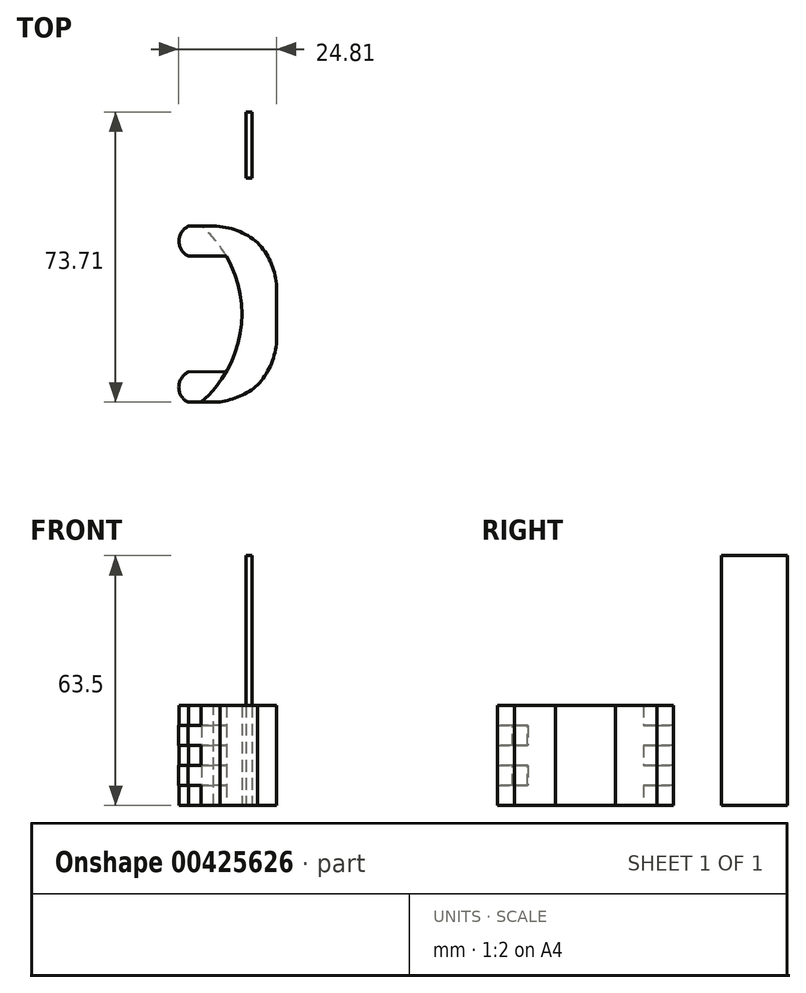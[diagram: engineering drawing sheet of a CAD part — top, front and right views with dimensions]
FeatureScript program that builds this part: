
annotation { "Feature Type Name" : "Feature", "Feature Type Description" : "" }
export const myFeature = defineFeature(function(context is Context, id is Id, definition is map)
    precondition{}
    {
        {
            var Q0;
            Q0=qCreatedBy(makeId("Top.planeOp"),FACE);
            var sketch = newSketch(context, id + "F0", { "sketchPlane" : qUnion([Q0])});
            skLineSegment(sketch, "E0.bottom", {"start": v(-27.3, 5.1) * mm, "end": v(-25.7, 5.1) * mm});
            skLineSegment(sketch, "E0.top", {"start": v(-27.3, -11.7) * mm, "end": v(-25.7, -11.7) * mm});
            skLineSegment(sketch, "E0.left", {"start": v(-27.3, 5.1) * mm, "end": v(-27.3, -11.7) * mm});
            skLineSegment(sketch, "E0.right", {"start": v(-25.7, 5.1) * mm, "end": v(-25.7, -11.7) * mm});
            skSolve(sketch);
        }
        {
            var Q0;
            Q0=makeQuery(id+"F0.imprint","IMPRINT",FACE,{"disambiguationData":[TD([[makeQuery(id+"F0.imprint","IMPRINT",EDGE,{"derivedFrom":sQuery(id+"F0.wireOp",EDGE,"E0.bottom")}),-1.0]])]});
            extrude(context, id + "F1", {"entities" : qUnion([Q0]), "depth" : 63.5 * mm});
        }
        {
            var Q0;
            Q0=qCreatedBy(makeId("Top.planeOp"),FACE);
            var sketch = newSketch(context, id + "F2", { "sketchPlane" : qUnion([Q0])});
            skArc(sketch, "E1", {"start": v(-38.65, -68.58) * mm, "mid": v(-28.33, -46.25) * mm, "end": v(-38.59, -23.9) * mm});
            skLineSegment(sketch, "E2", {"start": v(-28.33, -46.53) * mm, "end": v(-37.98, -46.37) * mm});
            skPoint(sketch, "E2.startSnap0", {"position": v(-38.5, -46.53) * mm});
            skPoint(sketch, "E2.endSnap0", {"position": v(-37.98, -46.54) * mm});
            skLineSegment(sketch, "E3", {"start": v(-29.06, -23.9) * mm, "end": v(-19.55, -32.32) * mm});
            skLineSegment(sketch, "E4", {"start": v(-29.13, -68.46) * mm, "end": v(-19.6, -60.08) * mm});
            skLineSegment(sketch, "E5", {"start": v(-38.59, -23.9) * mm, "end": v(-29.06, -23.9) * mm});
            skArc(sketch, "E6", {"start": v(-160.47, -81.65) * mm, "mid": v(-150.15, -59.32) * mm, "end": v(-160.4, -36.97) * mm});
            skLineSegment(sketch, "E7", {"start": v(-150.15, -59.6) * mm, "end": v(-159.8, -59.44) * mm});
            skPoint(sketch, "E7.startSnap0", {"position": v(-160.31, -59.6) * mm});
            skPoint(sketch, "E7.endSnap0", {"position": v(-159.8, -59.6) * mm});
            skLineSegment(sketch, "E8", {"start": v(-141.36, -36.97) * mm, "end": v(-141.42, -81.42) * mm});
            skLineSegment(sketch, "E9", {"start": v(-160.47, -81.65) * mm, "end": v(-141.42, -81.42) * mm});
            skLineSegment(sketch, "E10", {"start": v(-150.88, -36.97) * mm, "end": v(-141.37, -45.39) * mm});
            skLineSegment(sketch, "E11", {"start": v(-150.95, -81.53) * mm, "end": v(-141.4, -73.15) * mm});
            skLineSegment(sketch, "E12", {"start": v(-160.4, -36.97) * mm, "end": v(-150.88, -36.97) * mm});
            skLineSegment(sketch, "E13", {"start": v(-38.65, -68.58) * mm, "end": v(-29.13, -68.46) * mm});
            skLineSegment(sketch, "E14", {"start": v(-19.6, -60.08) * mm, "end": v(-19.55, -32.32) * mm});
            skSolve(sketch);
        }
        {
            var Q0;
            Q0=makeQuery(id+"F2.imprint","IMPRINT",FACE,{"disambiguationData":[TD([[makeQuery(id+"F2.imprint","IMPRINT",EDGE,{"derivedFrom":sQuery(id+"F2.wireOp",EDGE,"E3")}),-1.0]])]});
            extrude(context, id + "F3", {"entities" : qUnion([Q0]), "depth" : 25.4 * mm});
        }
        {
            var Q0;
            Q0=makeQuery(id+"F3.opExtrude","SWEPT_FACE",FACE,{"disambiguationData":[OSD([sQuery(id+"F2.wireOp",EDGE,"E13")])]});
            var sketch = newSketch(context, id + "F4", { "sketchPlane" : qUnion([Q0])});
            skLineSegment(sketch, "E15.bottom", {"start": v(-29.92, 25.4) * mm, "end": v(-45.16, 25.4) * mm});
            skLineSegment(sketch, "E15.top", {"start": v(-29.92, 20.32) * mm, "end": v(-45.16, 20.32) * mm});
            skLineSegment(sketch, "E15.left", {"start": v(-29.92, 25.4) * mm, "end": v(-29.92, 20.32) * mm});
            skLineSegment(sketch, "E15.right", {"start": v(-45.16, 25.4) * mm, "end": v(-45.16, 20.32) * mm});
            skLineSegment(sketch, "E16.top", {"start": v(-29.92, 15.24) * mm, "end": v(-45.16, 15.24) * mm});
            skLineSegment(sketch, "E16.left", {"start": v(-29.92, 20.32) * mm, "end": v(-29.92, 15.24) * mm});
            skLineSegment(sketch, "E16.right", {"start": v(-45.16, 20.32) * mm, "end": v(-45.16, 15.24) * mm});
            skLineSegment(sketch, "E17.top", {"start": v(-29.92, 10.16) * mm, "end": v(-45.16, 10.16) * mm});
            skLineSegment(sketch, "E17.left", {"start": v(-29.92, 15.24) * mm, "end": v(-29.92, 10.16) * mm});
            skLineSegment(sketch, "E17.right", {"start": v(-45.16, 15.24) * mm, "end": v(-45.16, 10.16) * mm});
            skLineSegment(sketch, "E18.top", {"start": v(-29.92, 5.08) * mm, "end": v(-45.16, 5.08) * mm});
            skLineSegment(sketch, "E18.left", {"start": v(-29.92, 10.16) * mm, "end": v(-29.92, 5.08) * mm});
            skLineSegment(sketch, "E18.right", {"start": v(-45.16, 10.16) * mm, "end": v(-45.16, 5.08) * mm});
            skLineSegment(sketch, "E19.top", {"start": v(-29.92, 0) * mm, "end": v(-45.16, 0) * mm});
            skLineSegment(sketch, "E19.left", {"start": v(-29.92, 5.08) * mm, "end": v(-29.92, 0) * mm});
            skLineSegment(sketch, "E19.right", {"start": v(-45.16, 5.08) * mm, "end": v(-45.16, 0) * mm});
            skSolve(sketch);
        }
        {
            var Q0;
            Q0=makeQuery(id+"F3.opExtrude","SWEPT_FACE",FACE,{"disambiguationData":[OSD([sQuery(id+"F2.wireOp",EDGE,"E5")])]});
            var sketch = newSketch(context, id + "F5", { "sketchPlane" : qUnion([Q0])});
            skLineSegment(sketch, "E20.bottom", {"start": v(29.06, 25.4) * mm, "end": v(44.3, 25.4) * mm});
            skLineSegment(sketch, "E20.top", {"start": v(29.06, 20.32) * mm, "end": v(44.3, 20.32) * mm});
            skLineSegment(sketch, "E20.left", {"start": v(29.06, 25.4) * mm, "end": v(29.06, 20.32) * mm});
            skLineSegment(sketch, "E20.right", {"start": v(44.3, 25.4) * mm, "end": v(44.3, 20.32) * mm});
            skLineSegment(sketch, "E21.top", {"start": v(29.06, 15.24) * mm, "end": v(44.3, 15.24) * mm});
            skLineSegment(sketch, "E21.left", {"start": v(29.06, 20.32) * mm, "end": v(29.06, 15.24) * mm});
            skLineSegment(sketch, "E21.right", {"start": v(44.3, 20.32) * mm, "end": v(44.3, 15.24) * mm});
            skLineSegment(sketch, "E22.top", {"start": v(29.06, 10.16) * mm, "end": v(44.3, 10.16) * mm});
            skLineSegment(sketch, "E22.left", {"start": v(29.06, 15.24) * mm, "end": v(29.06, 10.16) * mm});
            skLineSegment(sketch, "E22.right", {"start": v(44.3, 15.24) * mm, "end": v(44.3, 10.16) * mm});
            skLineSegment(sketch, "E23.top", {"start": v(29.06, 5.08) * mm, "end": v(44.3, 5.08) * mm});
            skLineSegment(sketch, "E23.left", {"start": v(29.06, 10.16) * mm, "end": v(29.06, 5.08) * mm});
            skLineSegment(sketch, "E23.right", {"start": v(44.3, 10.16) * mm, "end": v(44.3, 5.08) * mm});
            skLineSegment(sketch, "E24.top", {"start": v(29.06, 0) * mm, "end": v(44.3, 0) * mm});
            skLineSegment(sketch, "E24.left", {"start": v(29.06, 5.08) * mm, "end": v(29.06, 0) * mm});
            skLineSegment(sketch, "E24.right", {"start": v(44.3, 5.08) * mm, "end": v(44.3, 0) * mm});
            skSolve(sketch);
        }
        {
            var Q0;
            {var subQ3=sQuery(id+"F5.wireOp",EDGE,"E20.left");Q0=makeQuery(id+"F5.imprint","IMPRINT",FACE,{"disambiguationData":[TD([[makeQuery(id+"F5.imprint","IMPRINT",EDGE,{"derivedFrom":subQ3}),1.0]])]});}
            var Q1;
            {var subQ3=sQuery(id+"F5.wireOp",EDGE,"E20.right");Q1=makeQuery(id+"F5.imprint","IMPRINT",FACE,{"disambiguationData":[TD([[makeQuery(id+"F5.imprint","IMPRINT",EDGE,{"derivedFrom":subQ3}),-1.0]])]});}
            var Q2;
            {var subQ0=sQuery(id+"F5.wireOp",EDGE,"E22.left");Q2=makeQuery(id+"F5.imprint","IMPRINT",FACE,{"disambiguationData":[TD([[makeQuery(id+"F5.imprint","IMPRINT",EDGE,{"derivedFrom":subQ0}),1.0]])]});}
            var Q3;
            {var subQ0=sQuery(id+"F5.wireOp",EDGE,"E22.right");Q3=makeQuery(id+"F5.imprint","IMPRINT",FACE,{"disambiguationData":[TD([[makeQuery(id+"F5.imprint","IMPRINT",EDGE,{"derivedFrom":subQ0}),-1.0]])]});}
            var Q4;
            {var subQ0=sQuery(id+"F5.wireOp",EDGE,"E24.left");Q4=makeQuery(id+"F5.imprint","IMPRINT",FACE,{"disambiguationData":[TD([[makeQuery(id+"F5.imprint","IMPRINT",EDGE,{"derivedFrom":subQ0}),1.0]])]});}
            var Q5;
            {var subQ0=sQuery(id+"F5.wireOp",EDGE,"E24.right");Q5=makeQuery(id+"F5.imprint","IMPRINT",FACE,{"disambiguationData":[TD([[makeQuery(id+"F5.imprint","IMPRINT",EDGE,{"derivedFrom":subQ0}),-1.0]])]});}
            extrude(context, id + "F6", {"entities" : qUnion([Q0, Q1, Q2, Q3, Q4, Q5]), "operationType" : NewBodyOperationType.ADD, "oppositeDirection" : true, "depth" : 7.62 * mm, "offsetDistance" : 25.4 * mm});
        }
        {
            var Q0;
            {var subQ0=sQuery(id+"F2.wireOp",EDGE,"E4");var subQ1=sQuery(id+"F2.wireOp",EDGE,"E14");var subQ2=sQuery(id+"F2.wireOp",EDGE,"E13");var subQ3=sQuery(id+"F2.wireOp",EDGE,"E1");var subQ4=sQuery(id+"F2.wireOp",EDGE,"E5");var subQ5=sQuery(id+"F2.wireOp",EDGE,"E3");Q0=makeQuery(id+"F6.boolean.opBoolean","MERGE",FACE,{"derivedFrom":[makeQuery(id+"FHbpOmhKajvLCAy_13.boolean.opBoolean","SPLIT",FACE,{"disambiguationData":[TD([makeQuery(id+"F3.opExtrude","SWEPT_FACE",FACE,{"disambiguationData":[OSD([subQ3])]})])],"derivedFrom":makeQuery(id+"F3.opExtrude","CAP_FACE",FACE,{"disambiguationData":[OSD([subQ3,subQ5,subQ0,subQ4,subQ2,subQ1])],"isStart":false})}),makeQuery(id+"F6.opExtrude","SWEPT_FACE",FACE,{"disambiguationData":[OSD([sQuery(id+"F5.wireOp",EDGE,"E20.bottom")])]})]});}
            var sketch = newSketch(context, id + "F7", { "sketchPlane" : qUnion([Q0])});
            skLineSegment(sketch, "E25.bottom", {"start": v(-41.89, -23.9) * mm, "end": v(-44.3, -23.9) * mm});
            skLineSegment(sketch, "E25.top", {"start": v(-41.89, -31.52) * mm, "end": v(-44.3, -31.52) * mm});
            skLineSegment(sketch, "E25.left", {"start": v(-41.89, -23.9) * mm, "end": v(-41.89, -31.52) * mm});
            skLineSegment(sketch, "E25.right", {"start": v(-44.3, -23.9) * mm, "end": v(-44.3, -31.52) * mm});
            skArc(sketch, "E26", {"start": v(-41.89, -23.9) * mm, "mid": v(-43.65, -25.46) * mm, "end": v(-44.3, -27.71) * mm});
            skArc(sketch, "E27", {"start": v(-44.3, -27.71) * mm, "mid": v(-43.65, -29.97) * mm, "end": v(-41.89, -31.52) * mm});
            skSolve(sketch);
        }
        {
            var Q0;
            {var subQ0=sQuery(id+"F7.wireOp",EDGE,"E25.bottom");Q0=makeQuery(id+"F7.imprint","IMPRINT",FACE,{"disambiguationData":[TD([[makeQuery(id+"F7.imprint","IMPRINT",EDGE,{"derivedFrom":subQ0}),-1.0]])]});}
            var Q1;
            {var subQ0=sQuery(id+"F7.wireOp",EDGE,"E25.top");Q1=makeQuery(id+"F7.imprint","IMPRINT",FACE,{"disambiguationData":[TD([[makeQuery(id+"F7.imprint","IMPRINT",EDGE,{"derivedFrom":subQ0}),1.0]])]});}
            extrude(context, id + "F8", {"entities" : qUnion([Q0, Q1]), "operationType" : NewBodyOperationType.REMOVE, "oppositeDirection" : true, "depth" : 30.48 * mm, "offsetDistance" : 25.4 * mm});
        }
        {
            var Q0;
            {var subQ0=sQuery(id+"F4.wireOp",EDGE,"E16.left");Q0=makeQuery(id+"F4.imprint","IMPRINT",FACE,{"disambiguationData":[TD([[makeQuery(id+"F4.imprint","IMPRINT",EDGE,{"derivedFrom":subQ0}),-1.0]])]});}
            var Q1;
            {var subQ0=sQuery(id+"F4.wireOp",EDGE,"E16.right");Q1=makeQuery(id+"F4.imprint","IMPRINT",FACE,{"disambiguationData":[TD([[makeQuery(id+"F4.imprint","IMPRINT",EDGE,{"derivedFrom":subQ0}),1.0]])]});}
            var Q2;
            {var subQ0=sQuery(id+"F4.wireOp",EDGE,"E18.left");Q2=makeQuery(id+"F4.imprint","IMPRINT",FACE,{"disambiguationData":[TD([[makeQuery(id+"F4.imprint","IMPRINT",EDGE,{"derivedFrom":subQ0}),-1.0]])]});}
            var Q3;
            {var subQ0=sQuery(id+"F4.wireOp",EDGE,"E18.right");Q3=makeQuery(id+"F4.imprint","IMPRINT",FACE,{"disambiguationData":[TD([[makeQuery(id+"F4.imprint","IMPRINT",EDGE,{"derivedFrom":subQ0}),1.0]])]});}
            extrude(context, id + "F9", {"entities" : qUnion([Q0, Q1, Q2, Q3]), "operationType" : NewBodyOperationType.ADD, "oppositeDirection" : true, "depth" : 7.62 * mm, "offsetDistance" : 25.4 * mm});
        }
        {
            var Q0;
            Q0=makeQuery(id+"F9.opExtrude","SWEPT_FACE",FACE,{"disambiguationData":[OSD([sQuery(id+"F4.wireOp",EDGE,"E15.top")])]});
            var sketch = newSketch(context, id + "F10", { "sketchPlane" : qUnion([Q0])});
            skLineSegment(sketch, "E28.bottom", {"start": v(-41.95, -61) * mm, "end": v(-44.37, -61) * mm});
            skLineSegment(sketch, "E28.top", {"start": v(-41.95, -68.64) * mm, "end": v(-44.37, -68.64) * mm});
            skLineSegment(sketch, "E28.left", {"start": v(-41.95, -61) * mm, "end": v(-41.95, -68.64) * mm});
            skLineSegment(sketch, "E28.right", {"start": v(-44.37, -61) * mm, "end": v(-44.37, -68.64) * mm});
            skArc(sketch, "E29", {"start": v(-41.95, -61) * mm, "mid": v(-43.72, -62.55) * mm, "end": v(-44.37, -64.82) * mm});
            skArc(sketch, "E30", {"start": v(-44.37, -64.82) * mm, "mid": v(-43.72, -67.08) * mm, "end": v(-41.95, -68.64) * mm});
            skLineSegment(sketch, "E31.bottom", {"start": v(-44.37, -61) * mm, "end": v(-44.45, -61) * mm});
            skLineSegment(sketch, "E31.top", {"start": v(-44.37, -68.64) * mm, "end": v(-44.45, -68.64) * mm});
            skLineSegment(sketch, "E31.right", {"start": v(-44.45, -61) * mm, "end": v(-44.45, -68.64) * mm});
            skSolve(sketch);
        }
        {
            var Q0;
            {var subQ0=sQuery(id+"F10.wireOp",EDGE,"E29");Q0=makeQuery(id+"F10.imprint","IMPRINT",FACE,{"disambiguationData":[TD([[makeQuery(id+"F10.imprint","IMPRINT",EDGE,{"derivedFrom":subQ0}),-1.0]])]});}
            var Q1;
            {var subQ0=sQuery(id+"F10.wireOp",EDGE,"E28.right");var subQ1=sQuery(id+"F10.wireOp",EDGE,"E30");var subQ2=makeQuery(id+"F10.imprint","INTERSECT",VERTEX,{"derivedFrom":[subQ1,subQ0]});Q1=makeQuery(id+"F10.imprint","IMPRINT",FACE,{"disambiguationData":[TD([[makeQuery(id+"F10.imprint","IMPRINT",EDGE,{"disambiguationData":[TD([[subQ2,-1.0]])],"derivedFrom":subQ1}),-1.0]])]});}
            var Q2;
            {var subQ6=sQuery(id+"F10.wireOp",EDGE,"E28.right");var subQ10=makeQuery(id+"F10.imprint","INTERSECT",VERTEX,{"derivedFrom":[sQuery(id+"F10.wireOp",EDGE,"E29"),subQ6]});Q2=makeQuery(id+"F10.imprint","IMPRINT",FACE,{"disambiguationData":[TD([[makeQuery(id+"F10.imprint","IMPRINT",EDGE,{"disambiguationData":[TD([[subQ10,1.0]])],"derivedFrom":subQ6}),-1.0]])]});}
            extrude(context, id + "F11", {"entities" : qUnion([Q0, Q1, Q2]), "operationType" : NewBodyOperationType.REMOVE, "oppositeDirection" : true, "depth" : 25.4 * mm, "offsetDistance" : 25.4 * mm});
        }
        {
            var Q0;
            Q0=makeQuery(id+"F6.boolean.opBoolean","MERGE",FACE,{"derivedFrom":[makeQuery(id+"F3.opExtrude","CAP_FACE",FACE,{"disambiguationData":[OSD([sQuery(id+"F2.wireOp",EDGE,"E1"),sQuery(id+"F2.wireOp",EDGE,"E3"),sQuery(id+"F2.wireOp",EDGE,"E4"),sQuery(id+"F2.wireOp",EDGE,"E5"),sQuery(id+"F2.wireOp",EDGE,"E13"),sQuery(id+"F2.wireOp",EDGE,"E14")])],"isStart":false}),makeQuery(id+"F6.opExtrude","SWEPT_FACE",FACE,{"disambiguationData":[OSD([sQuery(id+"F5.wireOp",EDGE,"E20.bottom")])]})]});
            var sketch = newSketch(context, id + "F12", { "sketchPlane" : qUnion([Q0])});
            skArc(sketch, "E32", {"start": v(-24.3, -28.11) * mm, "mid": v(-29.53, -25.04) * mm, "end": v(-35.47, -23.9) * mm});
            skPoint(sketch, "E33.startSnap0", {"position": v(-33.89, -68.52) * mm});
            skLineSegment(sketch, "E34", {"start": v(-19.57, -46.2) * mm, "end": v(-19.56, -38.58) * mm});
            skLineSegment(sketch, "E35", {"start": v(-19.57, -46.2) * mm, "end": v(-19.58, -53.82) * mm});
            skArc(sketch, "E36", {"start": v(-19.56, -38.58) * mm, "mid": v(-21.06, -32.95) * mm, "end": v(-24.3, -28.11) * mm});
            skArc(sketch, "E37", {"start": v(-24.36, -64.27) * mm, "mid": v(-21.1, -59.44) * mm, "end": v(-19.58, -53.82) * mm});
            skLineSegment(sketch, "E38.bottom", {"start": v(-41.89, -31.52) * mm, "end": v(-35.47, -31.52) * mm});
            skLineSegment(sketch, "E38.top", {"start": v(-41.89, -23.9) * mm, "end": v(-35.47, -23.9) * mm});
            skLineSegment(sketch, "E38.left", {"start": v(-41.89, -31.52) * mm, "end": v(-41.89, -23.9) * mm});
            skLineSegment(sketch, "E38.right", {"start": v(-35.47, -31.52) * mm, "end": v(-35.47, -23.9) * mm});
            skArc(sketch, "E39", {"start": v(-33.89, -68.52) * mm, "mid": v(-28.8, -67.11) * mm, "end": v(-24.36, -64.27) * mm});
            skSolve(sketch);
        }
        {
            var Q0;
            {var subQ0=sQuery(id+"F12.wireOp",EDGE,"E32");Q0=makeQuery(id+"F12.imprint","IMPRINT",FACE,{"disambiguationData":[TD([[makeQuery(id+"F12.imprint","IMPRINT",EDGE,{"derivedFrom":subQ0}),-1.0]])]});}
            var Q1;
            {var subQ0=sQuery(id+"F12.wireOp",EDGE,"E36");Q1=makeQuery(id+"F12.imprint","IMPRINT",FACE,{"disambiguationData":[TD([[makeQuery(id+"F12.imprint","IMPRINT",EDGE,{"derivedFrom":subQ0}),-1.0]])]});}
            var Q2;
            {var subQ0=sQuery(id+"F12.wireOp",EDGE,"E37");Q2=makeQuery(id+"F12.imprint","IMPRINT",FACE,{"disambiguationData":[TD([[makeQuery(id+"F12.imprint","IMPRINT",EDGE,{"derivedFrom":subQ0}),-1.0]])]});}
            var Q3;
            {var subQ0=sQuery(id+"F12.wireOp",EDGE,"E39");Q3=makeQuery(id+"F12.imprint","IMPRINT",FACE,{"disambiguationData":[TD([[makeQuery(id+"F12.imprint","IMPRINT",EDGE,{"derivedFrom":subQ0}),-1.0]])]});}
            extrude(context, id + "F13", {"entities" : qUnion([Q0, Q1, Q2, Q3]), "operationType" : NewBodyOperationType.REMOVE, "oppositeDirection" : true, "depth" : 27.94 * mm, "offsetDistance" : 25.4 * mm});
        }
    });
